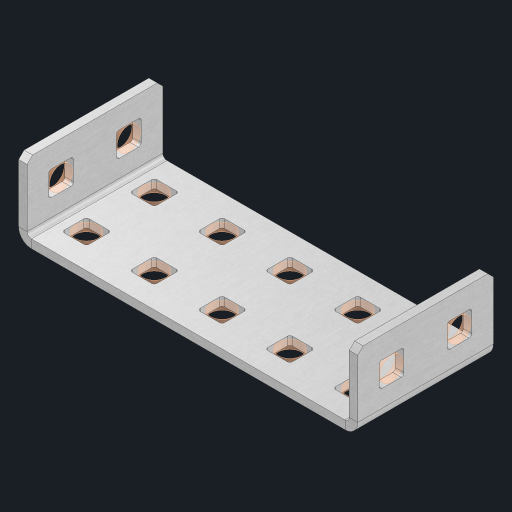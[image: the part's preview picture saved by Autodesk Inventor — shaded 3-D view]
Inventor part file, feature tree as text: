
AUTODESK INVENTOR PART (.ipt)
format: ipt  version: 2023 (Build 270158000, 158)  size: 484,864 bytes
history: native  units: in
note: dims shown in document units (in); Inventor stores cm internally (conversion verified against a paired STEP export)
features: other x19, extrude x13, sheet_metal_op x10, sketch x8, mirror x1, pattern_linear x1, chamfer x1
ambient origin geometry x8: Origin, YZ Plane, XZ Plane, XY Plane, X Axis, Y Axis, Z Axis, Center Point
bodies: Solid1 (feature_tree), Body (feature_tree)
feature tree (53):
  other  "Flange Pattern Plane"
  sheet_metal_op  "Flange Pattern"
  sheet_metal_op  "Body Pattern"
  other  "Arc Length"
  mirror  "Notch Mirror"
  pattern_linear  "Notch Pattern"  Spacing1=0.25in  [1 undecoded]
  chamfer  "End Chamfer"
  extrude  "Half Cut"  Depth=0.0625in
  sketch  "Sketch1"  dims[d0=2.5in]
  other  "Plate1"
  sketch  "Sketch2"  dims[d1=1.0in]
  other  "Plate2"
  sheet_metal_op  "Bend1"
  sheet_metal_op  "Corner1"
  sketch  "Sketch3"  dims[d2=0.0625in]
  other  "Flange Pattern Sketch"
  sketch  "Sketch7"  dims[d3=0.0625in]
  other  "Srf1"
  other  "Srf2"
  sketch  "Sketch8"  dims[d4=0.0312in]
  sketch  "Sketch9"  dims[d5=0.125in]
  other  "Srf91"
  sheet_metal_op  "Body Pattern Sketch"
  other  "Srf92"
  sketch  "Sketch13"  dims[d6=0.0625in]
  sketch  "Sketch14"  dims[d7=0.5in d8=90.0deg d9=0.0312in d10=0.25in d11=0.0625in d12=0.0625in d16=0.182in d17=0.02in d18=0.0625in d19=0.0in d20=0.25in d21=0.25in d46=0.172in d47=1.0in d48=0.0in d49=0.182in d50=0.02in d51=0.25in d52=0.25in d53=0.0625in d54=0.0in d55=0.172in d56=1.0in d57=0.0in d60=0.7874in d62=0.5in d63=1.9685in d65=0.5in d85=0.1473in d86=0.1782in d88=0.04in d89=0.0625in d90=0.0in d91=0.04in d92=0.0491in d95=2.5in d96=0.04in d97=0.25in d98=45.0deg d101=0.0in d102=2.497in d131=2.5in d132=0.7874in d134=0.5in d139=0.5in]
  other  "Srf856"
  other  "Srf1310"
  other  "Srf1311"
  other  "Srf1376"
  other  "Srf1377"
  other  "Srf1755"
  other  "Srf1942"
  other  "Srf1943"
  other  "Srf1944"
  other  "Srf1945"
  sheet_metal_op  "Flange Stamp"
  sheet_metal_op  "Flange Circle"
  sheet_metal_op  "Body Stamp"
  sheet_metal_op  "Body Circle"
  sheet_metal_op  "Notch"
  extrude  "ExtrusionSrf2"  Depth=0.0625in
  extrude  "ExtrusionSrf92"  Depth=0.182in
  extrude  "ExtrusionSrf856"  Depth=0.02in
  extrude  "ExtrusionSrf1310"  Depth=0.0625in
  extrude  "ExtrusionSrf1311"  TaperAngle=0.0deg  [1 undecoded]
  extrude  "ExtrusionSrf1376"  Depth=0.25in
  extrude  "ExtrusionSrf1377"  Depth=0.25in
  extrude  "ExtrusionSrf1755"  Depth=0.5in
  extrude  "ExtrusionSrf1942"  Depth=1.0in TaperAngle=0.0deg
  extrude  "ExtrusionSrf1943"  Depth=0.182in
  extrude  "ExtrusionSrf1944"  Depth=0.02in
  extrude  "ExtrusionSrf1945"  Depth=0.25in
note: 2 required parameter values undecoded (feature->parameter linkage not recoverable at this tier; creation-order binding heuristic only, values carry confidence <= 0.55)
